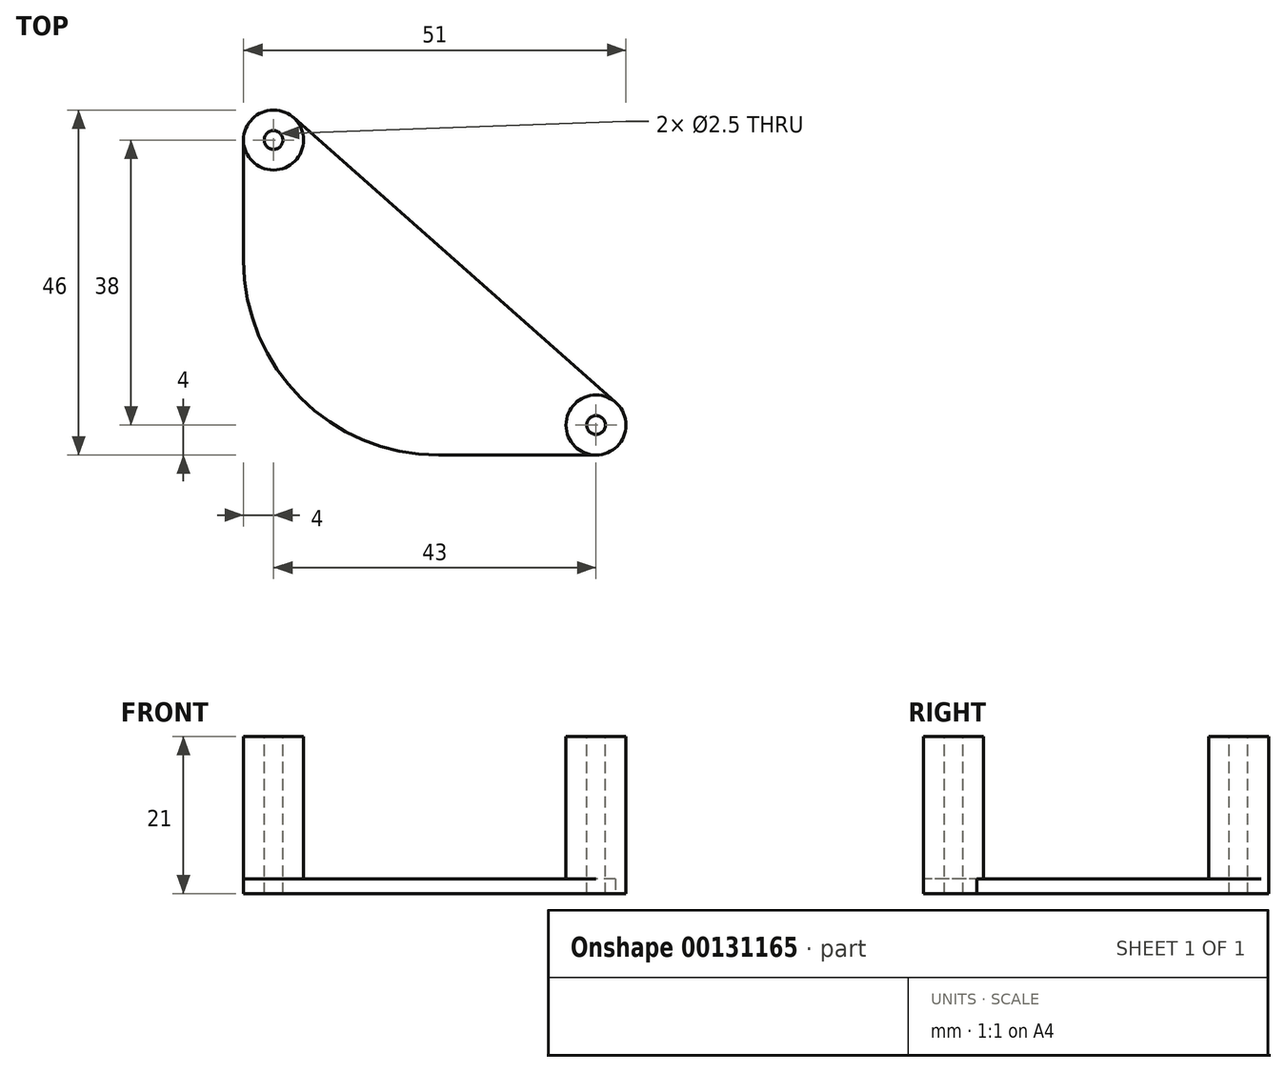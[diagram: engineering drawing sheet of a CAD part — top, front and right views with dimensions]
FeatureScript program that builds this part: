
annotation { "Feature Type Name" : "Feature", "Feature Type Description" : "" }
export const myFeature = defineFeature(function(context is Context, id is Id, definition is map)
    precondition{}
    {
        {
            var Q0;
            Q0=qCreatedBy(makeId("Top.planeOp"),FACE);
            var sketch = newSketch(context, id + "F0", { "sketchPlane" : qUnion([Q0])});
            skLineSegment(sketch, "E0.bottom", {"start": v(21.5, -19) * mm, "end": v(-21.5, -19) * mm, "construction": true});
            skLineSegment(sketch, "E0.top", {"start": v(21.5, 19) * mm, "end": v(-21.5, 19) * mm, "construction": true});
            skLineSegment(sketch, "E0.left", {"start": v(21.5, -19) * mm, "end": v(21.5, 19) * mm, "construction": true});
            skLineSegment(sketch, "E0.right", {"start": v(-21.5, -19) * mm, "end": v(-21.5, 19) * mm, "construction": true});
            skPoint(sketch, "E0.middle", {"position": v(0, 0) * mm});
            skLineSegment(sketch, "E1.right", {"start": v(-25.5, 19) * mm, "end": v(-25.5, -23) * mm});
            skCircle(sketch, "E2", {"center": v(-21.5, 19) * mm, "radius": 3.75 * mm, "construction": true});
            skCircle(sketch, "E3", {"center": v(21.5, -19) * mm, "radius": 3.75 * mm, "construction": true});
            skCircle(sketch, "E4", {"center": v(0, 0) * mm, "radius": 25.5 * mm, "construction": true});
            skCircle(sketch, "E5", {"center": v(21.5, -19) * mm, "radius": 4 * mm});
            skCircle(sketch, "E6", {"center": v(-21.5, 19) * mm, "radius": 4 * mm});
            skLineSegment(sketch, "E7", {"start": v(24.06, -15.92) * mm, "end": v(-18.85, 22) * mm});
            skLineSegment(sketch, "E8", {"start": v(21.5, -23) * mm, "end": v(-25.5, -23) * mm});
            skPoint(sketch, "E9.orphan", {"position": v(25.5, 25.5) * mm});
            skPoint(sketch, "E10.orphan", {"position": v(25.5, -25.5) * mm});
            skPoint(sketch, "E11.orphan", {"position": v(-25.5, -25.5) * mm});
            skPoint(sketch, "E12.orphan", {"position": v(-25.5, 25.5) * mm});
            skSolve(sketch);
        }
        {
            var Q0;
            Q0 = qSketchRegion(id + "F0", true);
            extrude(context, id + "F1", {"entities" : qUnion([Q0]), "depth" : 2 * mm});
        }
        {
            var Q0;
            Q0=makeQuery(id+"F1.opExtrude","CAP_FACE",FACE,{"disambiguationData":[OSD([sQuery(id+"F0.wireOp",EDGE,"E1.right"),sQuery(id+"F0.wireOp",EDGE,"E5"),sQuery(id+"F0.wireOp",EDGE,"E6"),sQuery(id+"F0.wireOp",EDGE,"E7"),sQuery(id+"F0.wireOp",EDGE,"E8")])],"isStart":false});
            var sketch = newSketch(context, id + "F2", { "sketchPlane" : qUnion([Q0])});
            skCircle(sketch, "E13", {"center": v(-21.5, 19) * mm, "radius": 4 * mm});
            skCircle(sketch, "E14", {"center": v(21.5, -19) * mm, "radius": 4 * mm});
            skSolve(sketch);
        }
        {
            var Q0;
            Q0 = qSketchRegion(id + "F2", true);
            extrude(context, id + "F3", {"entities" : qUnion([Q0]), "operationType" : NewBodyOperationType.ADD, "depth" : 19 * mm});
        }
        {
            var Q0;
            Q0=makeQuery(id+"F3.opExtrude","CAP_FACE",FACE,{"disambiguationData":[OSD([sQuery(id+"F2.wireOp",EDGE,"E13")])],"isStart":false});
            var sketch = newSketch(context, id + "F4", { "sketchPlane" : qUnion([Q0])});
            skCircle(sketch, "E15", {"center": v(-21.5, 19) * mm, "radius": 1.25 * mm});
            skSolve(sketch);
        }
        {
            var Q0;
            Q0 = qSketchRegion(id + "F4", true);
            extrude(context, id + "F5", {"entities" : qUnion([Q0]), "operationType" : NewBodyOperationType.REMOVE, "endBound" : BoundingType.THROUGH_ALL, "oppositeDirection" : true, "depth" : 25 * mm});
        }
        {
            var Q0;
            Q0=makeQuery(id+"F3.opExtrude","CAP_FACE",FACE,{"disambiguationData":[OSD([sQuery(id+"F2.wireOp",EDGE,"E14")])],"isStart":false});
            var sketch = newSketch(context, id + "F6", { "sketchPlane" : qUnion([Q0])});
            skCircle(sketch, "E16", {"center": v(21.5, -19) * mm, "radius": 1.25 * mm});
            skSolve(sketch);
        }
        {
            var Q0;
            Q0 = qSketchRegion(id + "F6", true);
            extrude(context, id + "F7", {"entities" : qUnion([Q0]), "operationType" : NewBodyOperationType.REMOVE, "endBound" : BoundingType.THROUGH_ALL, "oppositeDirection" : true, "depth" : 25 * mm});
        }
        {
            var Q0;
            Q0=makeQuery(id+"F1.opExtrude","SWEPT_EDGE",EDGE,{"disambiguationData":[OSD([sQuery(id+"F0.wireOp",EDGE,"E1.right"),sQuery(id+"F0.wireOp",EDGE,"E8")])]});
            fillet(context, id + "F8", {"entities" : qUnion([Q0]), "radius" : 26 * mm, "tangentPropagation" : true, "allowEdgeOverflow" : false});
        }
    });
